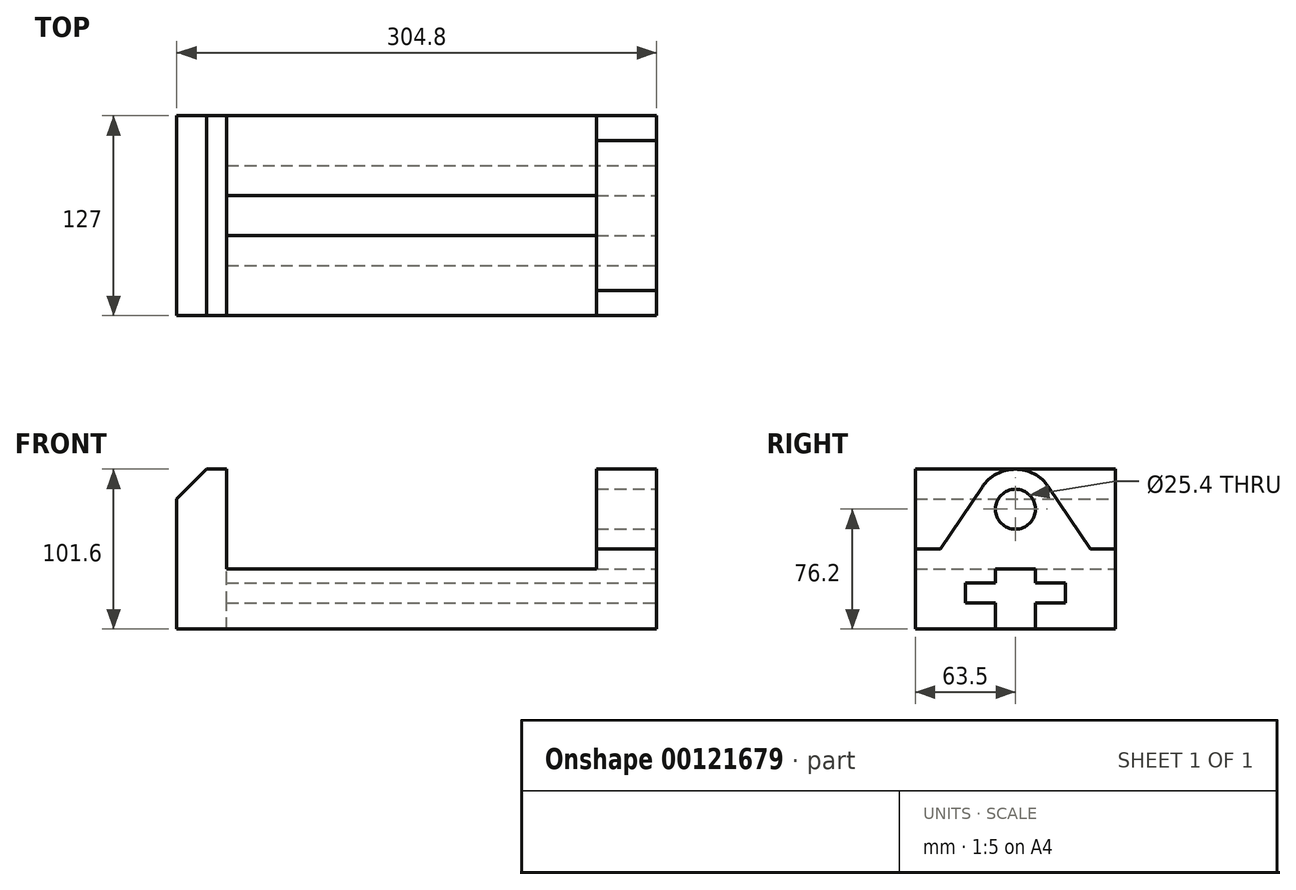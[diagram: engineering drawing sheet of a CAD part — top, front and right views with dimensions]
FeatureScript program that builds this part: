
annotation { "Feature Type Name" : "Feature", "Feature Type Description" : "" }
export const myFeature = defineFeature(function(context is Context, id is Id, definition is map)
    precondition{}
    {
        {
            var Q0;
            Q0=qCreatedBy(makeId("Front.planeOp"),FACE);
            var sketch = newSketch(context, id + "F0", { "sketchPlane" : qUnion([Q0])});
            skLineSegment(sketch, "E0", {"start": v(0, 0) * mm, "end": v(0, 101.6) * mm});
            skLineSegment(sketch, "E1", {"start": v(0, 101.6) * mm, "end": v(31.75, 101.6) * mm});
            skLineSegment(sketch, "E2", {"start": v(31.75, 101.6) * mm, "end": v(31.75, 38.1) * mm});
            skLineSegment(sketch, "E3", {"start": v(31.75, 38.1) * mm, "end": v(266.7, 38.1) * mm});
            skLineSegment(sketch, "E4", {"start": v(266.7, 38.1) * mm, "end": v(266.7, 101.6) * mm});
            skLineSegment(sketch, "E5", {"start": v(266.7, 101.6) * mm, "end": v(304.8, 101.6) * mm});
            skLineSegment(sketch, "E6", {"start": v(304.8, 101.6) * mm, "end": v(304.8, 0) * mm});
            skLineSegment(sketch, "E7", {"start": v(304.8, 0) * mm, "end": v(0, 0) * mm});
            skSolve(sketch);
        }
        {
            var Q0;
            Q0 = qSketchRegion(id + "F0", true);
            extrude(context, id + "F1", {"entities" : qUnion([Q0]), "endBound" : BoundingType.SYMMETRIC, "depth" : 127 * mm});
        }
        {
            var Q0;
            Q0=makeQuery(id+"F1.opExtrude","SWEPT_FACE",FACE,{"disambiguationData":[OSD([sQuery(id+"F0.wireOp",EDGE,"E6")])]});
            var sketch = newSketch(context, id + "F2", { "sketchPlane" : qUnion([Q0])});
            skLineSegment(sketch, "E8", {"start": v(-63.5, 0) * mm, "end": v(-63.5, 50.8) * mm});
            skLineSegment(sketch, "E9", {"start": v(-63.5, 50.8) * mm, "end": v(-47.63, 50.8) * mm});
            skLineSegment(sketch, "E10.MirrorCS", {"start": v(63.5, 0) * mm, "end": v(63.5, 50.8) * mm});
            skLineSegment(sketch, "E11", {"start": v(63.5, 50.8) * mm, "end": v(47.63, 50.8) * mm});
            skLineSegment(sketch, "E12", {"start": v(0, 0) * mm, "end": v(-12.7, 0) * mm});
            skLineSegment(sketch, "E13", {"start": v(0, 0) * mm, "end": v(12.7, 0) * mm});
            skLineSegment(sketch, "E14", {"start": v(-12.7, 0) * mm, "end": v(-12.7, 16.51) * mm});
            skLineSegment(sketch, "E15", {"start": v(-12.7, 16.51) * mm, "end": v(-31.75, 16.51) * mm});
            skLineSegment(sketch, "E16", {"start": v(-31.75, 16.51) * mm, "end": v(-31.75, 29.21) * mm});
            skLineSegment(sketch, "E17", {"start": v(-31.75, 29.21) * mm, "end": v(-12.7, 29.21) * mm});
            skLineSegment(sketch, "E18", {"start": v(-12.7, 29.21) * mm, "end": v(-12.7, 38.1) * mm});
            skLineSegment(sketch, "E19", {"start": v(-12.7, 38.1) * mm, "end": v(0, 38.1) * mm});
            skLineSegment(sketch, "E20.MirrorCS", {"start": v(12.7, 38.1) * mm, "end": v(0, 38.1) * mm});
            skLineSegment(sketch, "E21.MirrorCS", {"start": v(12.7, 29.21) * mm, "end": v(12.7, 38.1) * mm});
            skLineSegment(sketch, "E22.MirrorCS", {"start": v(31.75, 29.21) * mm, "end": v(12.7, 29.21) * mm});
            skLineSegment(sketch, "E23.MirrorCS", {"start": v(31.75, 16.51) * mm, "end": v(31.75, 29.21) * mm});
            skLineSegment(sketch, "E24.MirrorCS", {"start": v(12.7, 16.51) * mm, "end": v(31.75, 16.51) * mm});
            skLineSegment(sketch, "E25.MirrorCS", {"start": v(12.7, 0) * mm, "end": v(12.7, 16.51) * mm});
            skPoint(sketch, "E26.centerSnap0", {"position": v(0, 101.6) * mm});
            skCircle(sketch, "E27", {"center": v(0, 76.2) * mm, "radius": 12.7 * mm});
            skArc(sketch, "E28", {"start": v(21.1, 90.35) * mm, "mid": v(0, 101.6) * mm, "end": v(-21.1, 90.35) * mm});
            skLineSegment(sketch, "E29", {"start": v(-47.63, 50.8) * mm, "end": v(-21.1, 90.35) * mm});
            skLineSegment(sketch, "E30", {"start": v(47.63, 50.8) * mm, "end": v(21.1, 90.35) * mm});
            skSolve(sketch);
        }
        {
            var Q0;
            {var subQ5=sQuery(id+"F2.wireOp",EDGE,"E9");Q0=makeQuery(id+"F2.imprint","IMPRINT",FACE,{"disambiguationData":[TD([[makeQuery(id+"F2.imprint","IMPRINT",EDGE,{"derivedFrom":subQ5}),1.0]])]});}
            var Q1;
            {var subQ4=sQuery(id+"F2.wireOp",EDGE,"E11");Q1=makeQuery(id+"F2.imprint","IMPRINT",FACE,{"disambiguationData":[TD([[makeQuery(id+"F2.imprint","IMPRINT",EDGE,{"derivedFrom":subQ4}),-1.0]])]});}
            var Q2;
            Q2=makeQuery(id+"F2.imprint","IMPRINT",FACE,{"disambiguationData":[TD([[makeQuery(id+"F2.imprint","IMPRINT",EDGE,{"derivedFrom":sQuery(id+"F2.wireOp",EDGE,"E27")}),1.0]])]});
            extrude(context, id + "F3", {"entities" : qUnion([Q0, Q1, Q2]), "operationType" : NewBodyOperationType.REMOVE, "oppositeDirection" : true, "depth" : 38.1 * mm});
        }
        {
            var Q0;
            Q0=makeQuery(id+"F2.imprint","IMPRINT",FACE,{"disambiguationData":[TD([[makeQuery(id+"F2.imprint","IMPRINT",EDGE,{"derivedFrom":sQuery(id+"F2.wireOp",EDGE,"E12")}),1.0]])]});
            extrude(context, id + "F4", {"entities" : qUnion([Q0]), "operationType" : NewBodyOperationType.REMOVE, "oppositeDirection" : true, "depth" : 273.05 * mm});
        }
        {
            var Q0;
            Q0=makeQuery(id+"F1.opExtrude","SWEPT_EDGE",EDGE,{"disambiguationData":[OSD([sQuery(id+"F0.wireOp",EDGE,"E0"),sQuery(id+"F0.wireOp",EDGE,"E1")])]});
            chamfer(context, id + "F5", {"entities" : qUnion([Q0]), "width" : 19.05 * mm, "tangentPropagation" : true});
        }
    });
